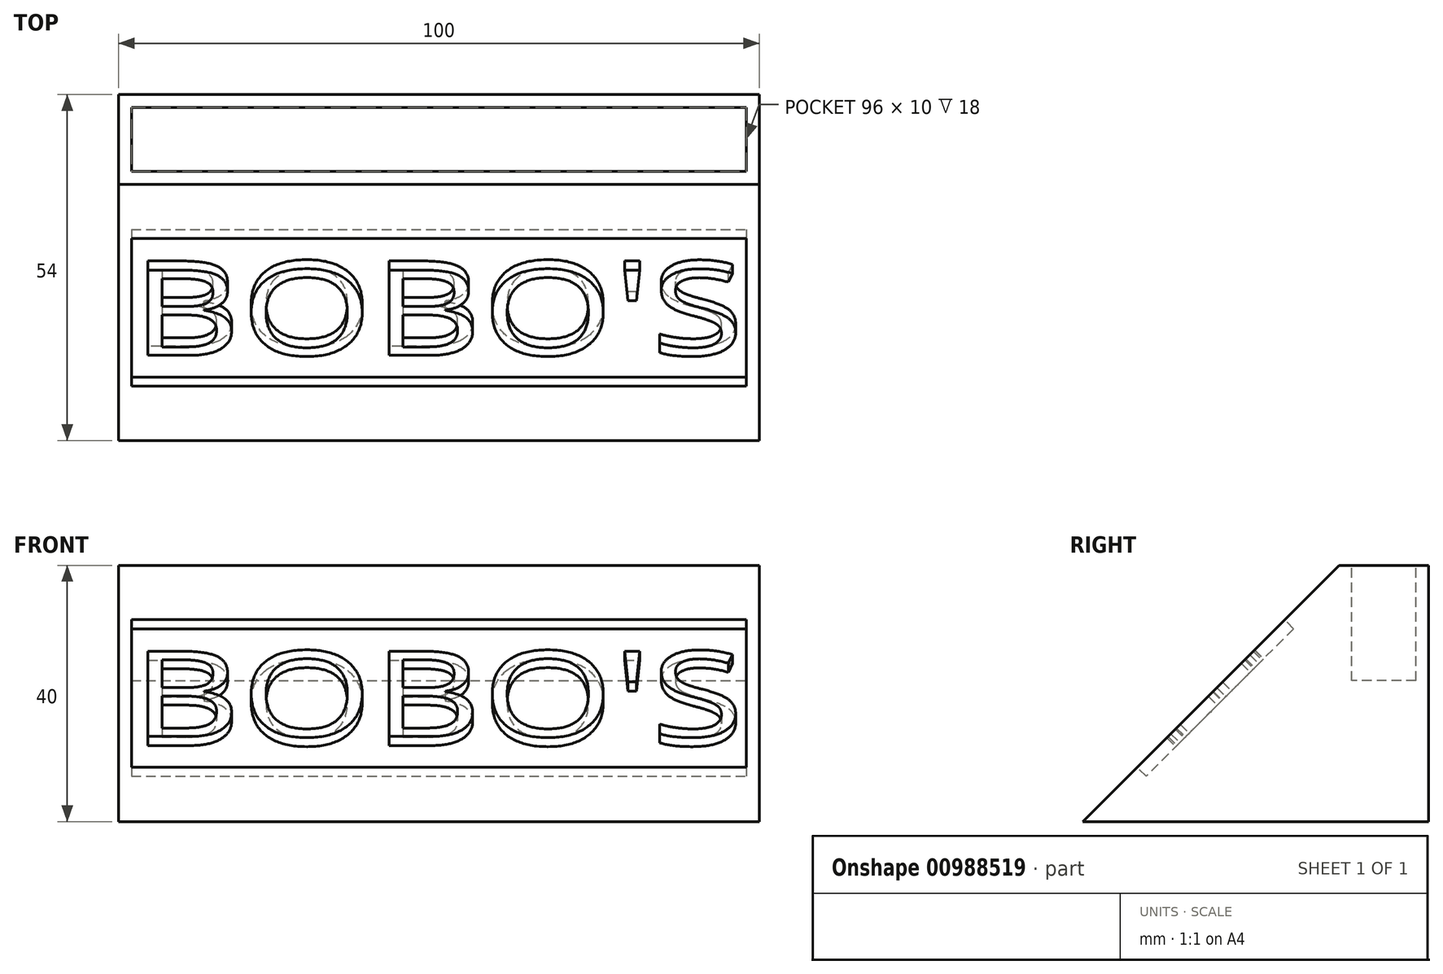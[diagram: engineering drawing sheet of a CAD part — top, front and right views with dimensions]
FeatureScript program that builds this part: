
annotation { "Feature Type Name" : "Feature", "Feature Type Description" : "" }
export const myFeature = defineFeature(function(context is Context, id is Id, definition is map)
    precondition{}
    {
        {
            var Q0;
            Q0=qCreatedBy(makeId("Top.planeOp"),FACE);
            var sketch = newSketch(context, id + "F0", { "sketchPlane" : qUnion([Q0])});
            skLineSegment(sketch, "E0.bottom", {"start": v(-50, -27) * mm, "end": v(50, -27) * mm});
            skLineSegment(sketch, "E0.top", {"start": v(-50, 27) * mm, "end": v(50, 27) * mm});
            skLineSegment(sketch, "E0.left", {"start": v(-50, -27) * mm, "end": v(-50, 27) * mm});
            skLineSegment(sketch, "E0.right", {"start": v(50, -27) * mm, "end": v(50, 27) * mm});
            skPoint(sketch, "E1", {"position": v(0, 27) * mm});
            skPoint(sketch, "E2", {"position": v(-50, 0) * mm});
            skSolve(sketch);
        }
        {
            var Q0;
            Q0=makeQuery(id+"F0.imprint","IMPRINT",FACE,{"disambiguationData":[TD([[makeQuery(id+"F0.imprint","IMPRINT",EDGE,{"derivedFrom":sQuery(id+"F0.wireOp",EDGE,"E0.bottom")}),1.0]])]});
            extrude(context, id + "F1", {"entities" : qUnion([Q0]), "depth" : 40 * mm, "offsetDistance" : 25 * mm});
        }
        {
            var Q0;
            Q0=makeQuery(id+"F1.opExtrude","SWEPT_FACE",FACE,{"disambiguationData":[OSD([sQuery(id+"F0.wireOp",EDGE,"E0.left")])]});
            var sketch = newSketch(context, id + "F2", { "sketchPlane" : qUnion([Q0])});
            skPoint(sketch, "E3", {"position": v(-13, 40) * mm});
            skLineSegment(sketch, "E4", {"start": v(-13, 40) * mm, "end": v(27, 0) * mm});
            skSolve(sketch);
        }
        {
            var Q0;
            {var subQ0=sQuery(id+"F2.wireOp",EDGE,"E4");Q0=makeQuery(id+"F2.imprint","IMPRINT",FACE,{"disambiguationData":[TD([[makeQuery(id+"F2.imprint","IMPRINT",EDGE,{"derivedFrom":subQ0}),1.0]])]});}
            var Q1;
            Q1 = qSketchRegion(id + "F4", true);
            extrude(context, id + "F3", {"entities" : qUnion([Q0, Q1]), "operationType" : NewBodyOperationType.REMOVE, "endBound" : BoundingType.UP_TO_NEXT, "oppositeDirection" : true, "depth" : 25 * mm, "offsetDistance" : 25 * mm});
        }
        {
            var Q0;
            Q0=makeQuery(id+"F3.boolean.opBoolean","COPY",FACE,{"derivedFrom":makeQuery(id+"F3.opExtrude","SWEPT_FACE",FACE,{"disambiguationData":[OSD([sQuery(id+"F2.wireOp",EDGE,"E4")])]})});
            var sketch = newSketch(context, id + "F4", { "sketchPlane" : qUnion([Q0])});
            skLineSegment(sketch, "E5.bottom", {"start": v(-48, 25.48) * mm, "end": v(48, 25.48) * mm});
            skLineSegment(sketch, "E5.top", {"start": v(-48, -7.1) * mm, "end": v(48, -7.1) * mm});
            skLineSegment(sketch, "E5.left", {"start": v(-48, 25.48) * mm, "end": v(-48, -7.1) * mm});
            skLineSegment(sketch, "E5.right", {"start": v(48, 25.48) * mm, "end": v(48, -7.1) * mm});
            skPoint(sketch, "E6", {"position": v(0, 25.48) * mm});
            skPoint(sketch, "E7", {"position": v(-48, 9.2) * mm});
            skPoint(sketch, "E8", {"position": v(-50, 9.2) * mm});
            skPoint(sketch, "E9", {"position": v(50, 9.2) * mm});
            skLineSegment(sketch, "E10", {"start": v(-50, 9.2) * mm, "end": v(50, 9.2) * mm, "construction": true});
            skSolve(sketch);
        }
        {
            var Q0;
            Q0 = qSketchRegion(id + "F4", true);
            extrude(context, id + "F5", {"entities" : qUnion([Q0]), "operationType" : NewBodyOperationType.REMOVE, "oppositeDirection" : true, "depth" : 2 * mm, "offsetDistance" : 25 * mm});
        }
        {
            var Q0;
            Q0=makeQuery(id+"F1.opExtrude","CAP_FACE",FACE,{"disambiguationData":[OSD([sQuery(id+"F0.wireOp",EDGE,"E0.bottom"),sQuery(id+"F0.wireOp",EDGE,"E0.top"),sQuery(id+"F0.wireOp",EDGE,"E0.left"),sQuery(id+"F0.wireOp",EDGE,"E0.right")])],"isStart":false});
            var sketch = newSketch(context, id + "F6", { "sketchPlane" : qUnion([Q0])});
            skLineSegment(sketch, "E11.bottom", {"start": v(-48, 25) * mm, "end": v(48, 25) * mm});
            skLineSegment(sketch, "E11.top", {"start": v(-48, 15) * mm, "end": v(48, 15) * mm});
            skLineSegment(sketch, "E11.left", {"start": v(-48, 25) * mm, "end": v(-48, 15) * mm});
            skLineSegment(sketch, "E11.right", {"start": v(48, 25) * mm, "end": v(48, 15) * mm});
            skLineSegment(sketch, "E12", {"start": v(50, 20) * mm, "end": v(-50, 20) * mm, "construction": true});
            skPoint(sketch, "E13", {"position": v(48, 20) * mm});
            skPoint(sketch, "E14", {"position": v(-48, 20) * mm});
            skPoint(sketch, "E15", {"position": v(0, 25) * mm});
            skSolve(sketch);
        }
        {
            var Q0;
            Q0 = qSketchRegion(id + "F6", true);
            extrude(context, id + "F7", {"entities" : qUnion([Q0]), "operationType" : NewBodyOperationType.REMOVE, "oppositeDirection" : true, "depth" : 18 * mm, "offsetDistance" : 25 * mm});
        }
        {
            var Q0;
            Q0=makeQuery(id+"F5.boolean.opBoolean","COPY",FACE,{"derivedFrom":makeQuery(id+"F5.opExtrude","CAP_FACE",FACE,{"disambiguationData":[OSD([sQuery(id+"F4.wireOp",EDGE,"E5.bottom"),sQuery(id+"F4.wireOp",EDGE,"E5.top"),sQuery(id+"F4.wireOp",EDGE,"E5.left"),sQuery(id+"F4.wireOp",EDGE,"E5.right")])],"isStart":false})});
            var sketch = newSketch(context, id + "F8", { "sketchPlane" : qUnion([Q0])});
            skText(sketch, "E16", { "text": "BOBO\'S", "fontName": "OpenSans-Regular.ttf"});
            skPoint(sketch, "E17", {"position": v(-48, 9.2) * mm});
            skLineSegment(sketch, "E18", {"start": v(-61.78, 9.2) * mm, "end": v(-48, 9.2) * mm});
            skPoint(sketch, "E18.endSnap0", {"position": v(48, 9.2) * mm});
            skLineSegment(sketch, "E19", {"start": v(-48, 9.2) * mm, "end": v(59.5, 9.2) * mm, "construction": true});
            skPoint(sketch, "E20", {"position": v(-48, -8.69) * mm});
            const initialGuessF8  = {"E16": [-0.048, -0.0003, 1, 0, 0.01899]};
            skSetInitialGuess(sketch, initialGuessF8);
            skSolve(sketch);
        }
        {
            var Q0;
            Q0 = qSketchRegion(id + "F8", true);
            extrude(context, id + "F9", {"entities" : qUnion([Q0]), "operationType" : NewBodyOperationType.ADD, "depth" : 2 * mm, "offsetDistance" : 25 * mm});
        }
    });
